# Revit family: Distanzmuffe sechskant, zn
name_source: partatom
category: HLS-Bauteile
revit_build: Autodesk Revit 2017 (Build: 20190507_1515(x64)
units: mm (PartAtom-declared; Revit-internal decimal feet)

## family parameters
Arbeitsebenenbasiert = Nein
Beim Laden mit Abzugskörper schneiden = Nein
Bemaßung runder Anschluss = Durchmesser verwenden
Gemeinsam genutzt = Ja
Immer vertikal = Nein
Raumberechnungspunkt = Nein
Teiletyp = Normal

## types (3) — shared parameters
Fabrikat = MEFA
Kurztext1 = Distanzmuffe sechskant
Material = Stahl
Mengeneinheit = St

## per-type parameters (varying)
| type | Artikelnummer | EAN | F2 | Gewicht | Gewicht pro Bauteil | H | Kurztext2 | Lochung | Länge | vpe |
| Distanzmuffe sechskant M10, zn | 0700104/zn | 4250928456458 | 9 mm | 0.06 kg | 0.06 kg | 40 mm  [stored 0.131234 ft] | Innengew. M10 L= 40 mm ZnNi | 4 mm  [stored 0.0131234 ft] | 40 mm  [stored 0.131234 ft] | 50 St |
| Distanzmuffe sechskant M12, zn | 0700123/zn | 4250928456625 | 9 mm | 0.05 kg | 0.05 kg | 40 mm  [stored 0.131234 ft] | Innengew. M12 L= 40 mm ZnNi | 5 mm  [stored 0.0164042 ft] | 40 mm  [stored 0.131234 ft] | 50 St |
| Distanzmuffe sechskant M16, zn | 0700167/zn | 4250928456632 | 12 mm  [stored 0.0393701 ft] | 0.14 kg | 0.14 kg | 50 mm  [stored 0.164042 ft] | Innengew. M16 L= 50 mm ZnNi | 7 mm  [stored 0.0229659 ft] | 50 mm  [stored 0.164042 ft] | 25 St |

note: [stored X ft] marks values corroborated as IEEE doubles in the binary element streams (Revit-internal decimal feet)

## geometry (parser evidence)
native form markers: Sweep x3
no freeform markers — native parametric forms only
